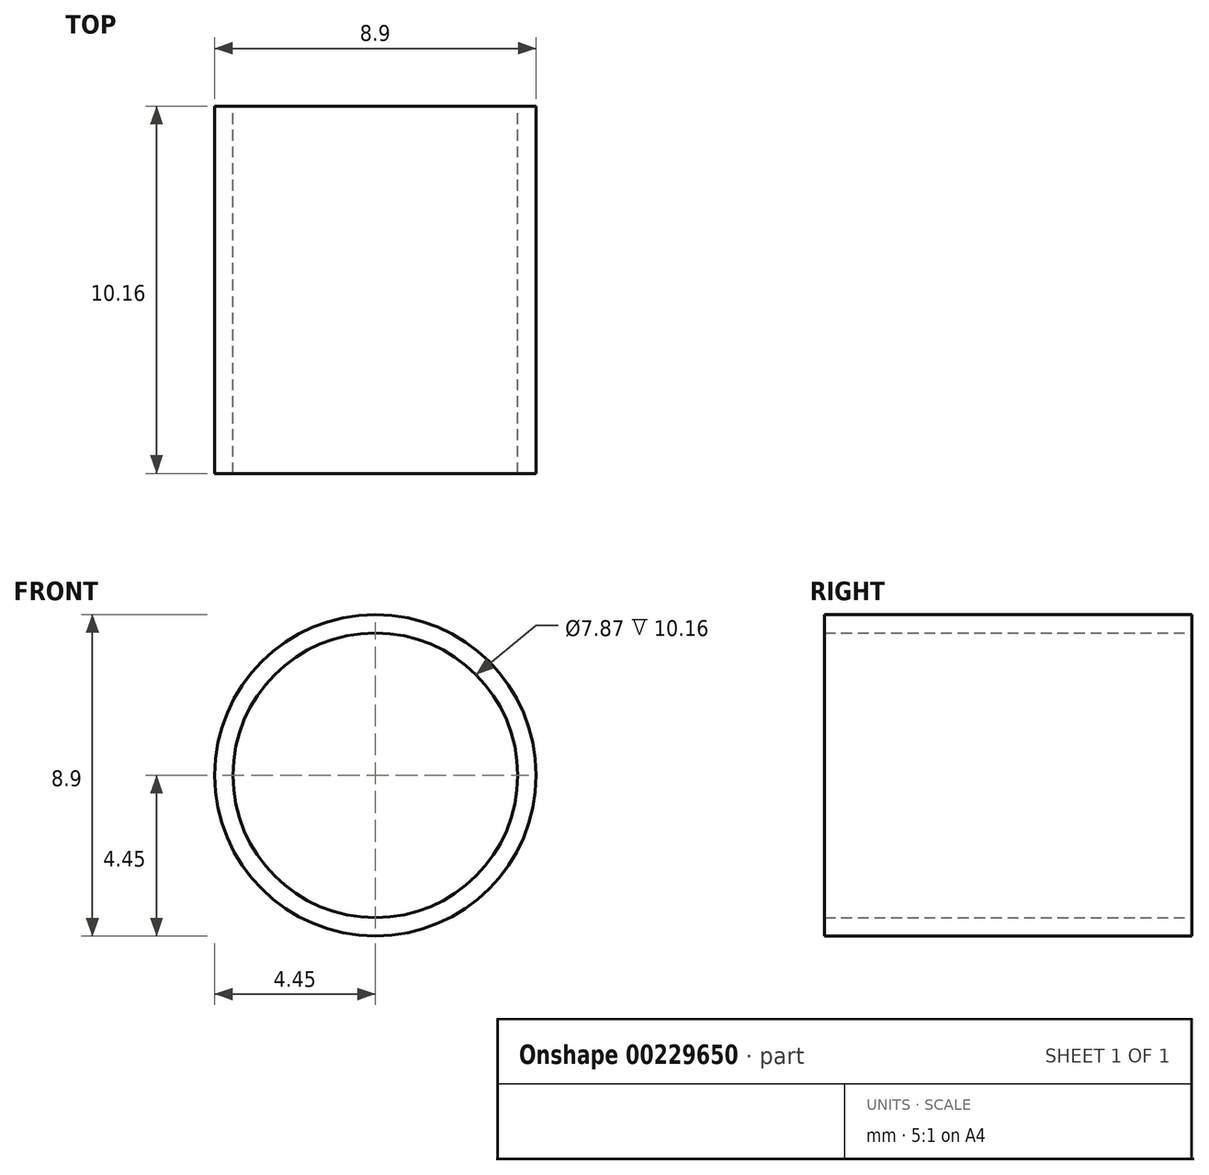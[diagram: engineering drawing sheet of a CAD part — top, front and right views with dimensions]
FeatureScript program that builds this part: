
annotation { "Feature Type Name" : "Feature", "Feature Type Description" : "" }
export const myFeature = defineFeature(function(context is Context, id is Id, definition is map)
    precondition{}
    {
        {
            var Q0;
            Q0=qCreatedBy(makeId("Front.planeOp"),FACE);
            var sketch = newSketch(context, id + "F0", { "sketchPlane" : qUnion([Q0])});
            skCircle(sketch, "E0", {"center": v(0, 0) * mm, "radius": 3.94 * mm});
            skCircle(sketch, "E1", {"center": v(0, 0) * mm, "radius": 4.45 * mm});
            skSolve(sketch);
        }
        {
            var Q0;
            Q0=makeQuery(id+"F0.imprint","IMPRINT",FACE,{"disambiguationData":[TD([[makeQuery(id+"F0.imprint","IMPRINT",EDGE,{"derivedFrom":sQuery(id+"F0.wireOp",EDGE,"E0")}),-1.0]])]});
            extrude(context, id + "F1", {"entities" : qUnion([Q0]), "depth" : 10.16 * mm});
        }
    });
